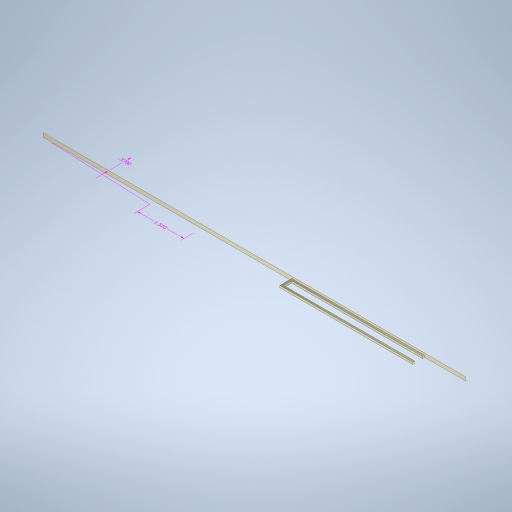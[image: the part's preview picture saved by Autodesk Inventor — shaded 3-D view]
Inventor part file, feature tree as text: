
AUTODESK INVENTOR PART (.ipt)
format: ipt  version: 2024.2 (Build 282272000, 272)  size: 274,944 bytes
history: native  units: in
note: dims shown in document units (in); Inventor stores cm internally (conversion verified against a paired STEP export)
features: other x3, plane x3, sketch x2, sweep x1
ambient origin geometry x8: Origin, YZ Plane, XZ Plane, XY Plane, X Axis, Y Axis, Z Axis, Center Point
bodies: Solid1 (feature_tree)
feature tree (9):
  other  "Annotations"
  sweep  "Sweep1"
  plane  "Work Plane1"
  plane  "Work Plane2"
  plane  "Work Plane4"
  sketch  "Sketch1"  dims[d6=0.0in d7=0.0in d11=0.25in d19=-0.25in]
  sketch  "Sketch2"  dims[d69=1.325in d70=1.325in d86=-0.1175in d89=0.1in d90=0.0in d91=0.0in d92=0.0in d98=0.02in d99=0.02in d42=0.2341in d43=0.169in d44=0.37in d48=0.2141in d49=0.2512in d50=1.51in]
  other  "Linear Dimension 1"
  other  "Linear Dimension 3"
